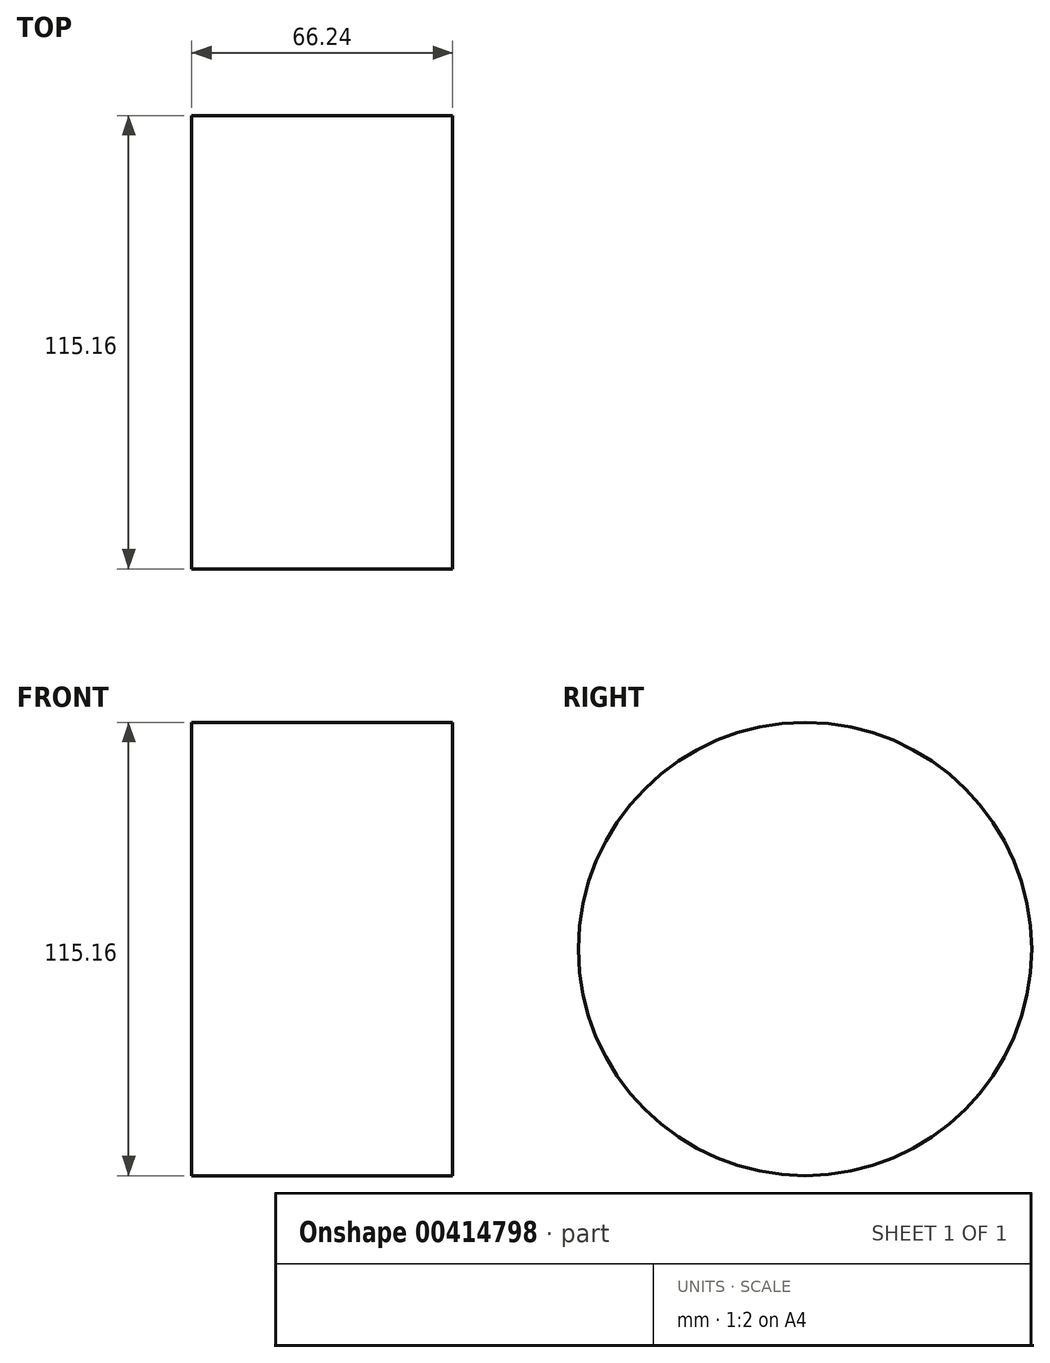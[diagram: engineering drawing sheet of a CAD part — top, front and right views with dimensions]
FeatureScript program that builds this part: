
annotation { "Feature Type Name" : "Feature", "Feature Type Description" : "" }
export const myFeature = defineFeature(function(context is Context, id is Id, definition is map)
    precondition{}
    {
        {
            var Q0;
            Q0=qCreatedBy(makeId("Front.planeOp"),FACE);
            var sketch = newSketch(context, id + "F0", { "sketchPlane" : qUnion([Q0])});
            skLineSegment(sketch, "E0.bottom", {"start": v(0, 0) * mm, "end": v(-66.24, 0) * mm});
            skLineSegment(sketch, "E0.top", {"start": v(0, 57.58) * mm, "end": v(-66.24, 57.58) * mm});
            skLineSegment(sketch, "E0.left", {"start": v(0, 0) * mm, "end": v(0, 57.58) * mm});
            skLineSegment(sketch, "E0.right", {"start": v(-66.24, 0) * mm, "end": v(-66.24, 57.58) * mm});
            skSolve(sketch);
        }
        {
            var Q0;
            Q0=makeQuery(id+"F0.imprint","IMPRINT",FACE,{"disambiguationData":[TD([[makeQuery(id+"F0.imprint","IMPRINT",EDGE,{"derivedFrom":sQuery(id+"F0.wireOp",EDGE,"E0.bottom")}),-1.0]])]});
            var Q1;
            Q1=sQuery(id+"F0.wireOp",EDGE,"E0.bottom");
            revolve(context, id + "F1", {"entities" : qUnion([Q0]), "axis" : qUnion([Q1]), "revolveType" : RevolveType.FULL});
        }
    });
